# Revit family: BFP-MAI-DSD-MS-___
name_source: partatom
category: Electrical Equipment
revit_build: Autodesk Revit 2018 (Build: 20181011_1500(x64)
units: mm (PartAtom-declared; Revit-internal decimal feet)

## family parameters
Cut with Voids When Loaded = No
Host = Face
OmniClass Number = 23.29.31.13.11
OmniClass Title = Main Fire Alarm Control Panels
Part Type = Other Panel
Room Calculation Point = No
Round Connector Dimension = Use Diameter
Shared = No

## types (2) — shared parameters
Default Elevation = 1219 mm
Panel Small R = 20 mm  [stored 0.0656168 ft]
r = 40 mm  [stored 0.131234 ft]
zero-valued in all types: DSD.BFP.Height, DSD.BFP.Length, DSD.BFP.Width

## per-type parameters (varying)
| type | High | Panel H1 | Panel Thick | Thick | Width | lock position | void1 | void1 h e | void1 h e+5 | void1 h s |
| 2/4/8/16 Zone | 370 mm  [stored 1.21391 ft] | 300 mm  [stored 0.984252 ft] | 128 mm  [stored 0.419948 ft] | 126 mm  [stored 0.413386 ft] | 325 mm  [stored 1.06627 ft] | 80 mm  [stored 0.262467 ft] | 328 mm  [stored 1.07612 ft] | 126 mm  [stored 0.413386 ft] | 131 mm  [stored 0.42979 ft] | 124 mm  [stored 0.406824 ft] |
| 32 Zone | 441 mm  [stored 1.44685 ft] | 371 mm  [stored 1.21719 ft] | 133 mm  [stored 0.436352 ft] | 131 mm  [stored 0.42979 ft] | 400 mm  [stored 1.31234 ft] | 153 mm  [stored 0.501969 ft] | 399 mm  [stored 1.30906 ft] | 131 mm  [stored 0.42979 ft] | 136 mm  [stored 0.446194 ft] | 129 mm  [stored 0.423228 ft] |

note: [stored X ft] marks values corroborated as IEEE doubles in the binary element streams (Revit-internal decimal feet)

## geometry (parser evidence)
native form markers: Sweep x14
no freeform markers — native parametric forms only
